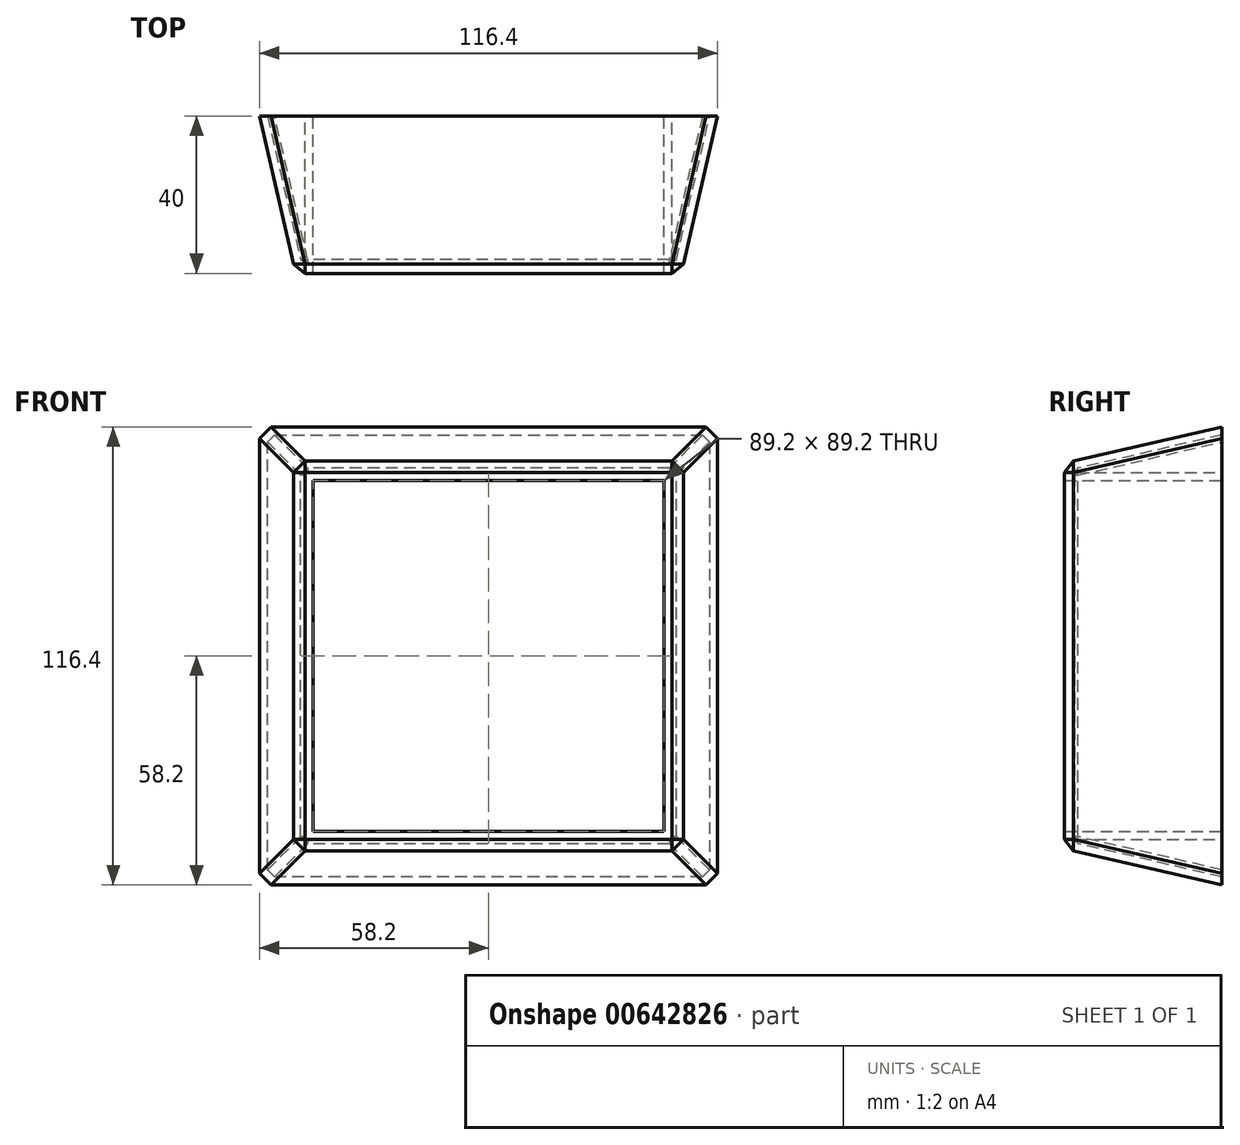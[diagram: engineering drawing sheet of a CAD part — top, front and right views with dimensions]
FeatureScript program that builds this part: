
annotation { "Feature Type Name" : "Feature", "Feature Type Description" : "" }
export const myFeature = defineFeature(function(context is Context, id is Id, definition is map)
    precondition{}
    {
        {
            var Q0;
            Q0=qCreatedBy(makeId("Front.planeOp"),FACE);
            var sketch = newSketch(context, id + "F0", { "sketchPlane" : qUnion([Q0])});
            skLineSegment(sketch, "E0.bottom", {"start": v(0, 116.4) * mm, "end": v(116.4, 116.4) * mm});
            skLineSegment(sketch, "E0.top", {"start": v(0, 0) * mm, "end": v(116.4, 0) * mm});
            skLineSegment(sketch, "E0.left", {"start": v(0, 116.4) * mm, "end": v(0, 0) * mm});
            skLineSegment(sketch, "E0.right", {"start": v(116.4, 116.4) * mm, "end": v(116.4, 0) * mm});
            skLineSegment(sketch, "E1.bottom", {"start": v(13.6, 102.8) * mm, "end": v(102.8, 102.8) * mm});
            skLineSegment(sketch, "E1.top", {"start": v(13.6, 13.6) * mm, "end": v(102.8, 13.6) * mm});
            skLineSegment(sketch, "E1.left", {"start": v(13.6, 102.8) * mm, "end": v(13.6, 13.6) * mm});
            skLineSegment(sketch, "E1.right", {"start": v(102.8, 102.8) * mm, "end": v(102.8, 13.6) * mm});
            skSolve(sketch);
        }
        {
            var Q0;
            Q0=makeQuery(id+"F0.imprint","IMPRINT",FACE,{"disambiguationData":[TD([[makeQuery(id+"F0.imprint","IMPRINT",EDGE,{"derivedFrom":sQuery(id+"F0.wireOp",EDGE,"E0.bottom")}),-1.0]])]});
            var Q1;
            Q1=makeQuery(id+"F0.imprint","IMPRINT",FACE,{"disambiguationData":[TD([[makeQuery(id+"F0.imprint","IMPRINT",EDGE,{"derivedFrom":sQuery(id+"F0.wireOp",EDGE,"E1.bottom")}),-1.0]])]});
            extrude(context, id + "F1", {"entities" : qUnion([Q0, Q1]), "depth" : 40 * mm, "offsetDistance" : 25 * mm, "hasDraft" : true, "draftAngle" : 13 * degree, "draftPullDirection" : true});
        }
        {
            var Q0;
            Q0=makeQuery(id+"F0.imprint","IMPRINT",FACE,{"disambiguationData":[TD([[makeQuery(id+"F0.imprint","IMPRINT",EDGE,{"derivedFrom":sQuery(id+"F0.wireOp",EDGE,"E1.bottom")}),-1.0]])]});
            extrude(context, id + "F2", {"entities" : qUnion([Q0]), "operationType" : NewBodyOperationType.REMOVE, "depth" : 40 * mm, "offsetDistance" : 25 * mm});
        }
        {
            var Q0;
            Q0=makeQuery(id+"F1.opExtrude","SWEPT_EDGE",EDGE,{"disambiguationData":[OSD([sQuery(id+"F0.wireOp",EDGE,"E0.top"),sQuery(id+"F0.wireOp",EDGE,"E0.left")])]});
            var Q1;
            Q1=makeQuery(id+"F1.opExtrude","SWEPT_EDGE",EDGE,{"disambiguationData":[OSD([sQuery(id+"F0.wireOp",EDGE,"E0.top"),sQuery(id+"F0.wireOp",EDGE,"E0.right")])]});
            var Q2;
            Q2=makeQuery(id+"F1.opExtrude","SWEPT_EDGE",EDGE,{"disambiguationData":[OSD([sQuery(id+"F0.wireOp",EDGE,"E0.bottom"),sQuery(id+"F0.wireOp",EDGE,"E0.right")])]});
            var Q3;
            Q3=makeQuery(id+"F1.opExtrude","SWEPT_EDGE",EDGE,{"disambiguationData":[OSD([sQuery(id+"F0.wireOp",EDGE,"E0.bottom"),sQuery(id+"F0.wireOp",EDGE,"E0.left")])]});
            var Q4;
            Q4=makeQuery(id+"F1.opExtrude","CAP_EDGE",EDGE,{"disambiguationData":[OSD([sQuery(id+"F0.wireOp",EDGE,"E0.right")])],"isStart":false});
            var Q5;
            Q5=makeQuery(id+"F1.opExtrude","CAP_EDGE",EDGE,{"disambiguationData":[OSD([sQuery(id+"F0.wireOp",EDGE,"E0.top")])],"isStart":false});
            var Q6;
            Q6=makeQuery(id+"F1.opExtrude","CAP_EDGE",EDGE,{"disambiguationData":[OSD([sQuery(id+"F0.wireOp",EDGE,"E0.left")])],"isStart":false});
            var Q7;
            Q7=makeQuery(id+"F1.opExtrude","CAP_EDGE",EDGE,{"disambiguationData":[OSD([sQuery(id+"F0.wireOp",EDGE,"E0.bottom")])],"isStart":false});
            chamfer(context, id + "F3", {"entities" : qUnion([Q0, Q1, Q2, Q3, Q4, Q5, Q6, Q7]), "width" : 3 * mm, "tangentPropagation" : true});
        }
        {
            var Q0;
            Q0=makeQuery(id+"F1.opExtrude","CAP_FACE",FACE,{"disambiguationData":[OSD([sQuery(id+"F0.wireOp",EDGE,"E0.bottom"),sQuery(id+"F0.wireOp",EDGE,"E0.top"),sQuery(id+"F0.wireOp",EDGE,"E0.left"),sQuery(id+"F0.wireOp",EDGE,"E0.right")])],"isStart":true});
            shell(context, id + "F4", {"entities" : qUnion([Q0]), "thickness" : 2 * mm});
        }
    });
